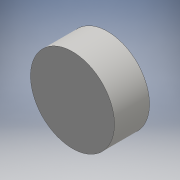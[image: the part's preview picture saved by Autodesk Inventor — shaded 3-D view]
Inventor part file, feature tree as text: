
AUTODESK INVENTOR PART (.ipt)
format: ipt  version: 2016 (Build 200138000, 138)  size: 86,528 bytes
history: native  units: mm
features: extrude x1, sketch x1
ambient origin geometry x8: Origin, YZ Plane, XZ Plane, XY Plane, X Axis, Y Axis, Z Axis, Center Point
bodies: Solid1 (feature_tree)
feature tree (2):
  extrude  "Extrusion1"  Depth=25.0mm TaperAngle=0.0deg
  sketch  "Sketch1"  dims[d0=60.0mm d1=25.0mm d2=0.0mm]
